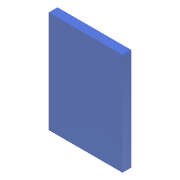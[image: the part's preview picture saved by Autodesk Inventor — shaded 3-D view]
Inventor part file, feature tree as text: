
AUTODESK INVENTOR PART (.ipt)
format: ipt  version: 2014 (Build 180170000, 170)  size: 67,072 bytes
history: native  units: mm
features: extrude x1, sketch x1
ambient origin geometry x8: Origin, YZ Plane, XZ Plane, XY Plane, X Axis, Y Axis, Z Axis, Center Point
bodies: Solid1 (feature_tree)
feature tree (2):
  extrude  "Extrusion1"  Depth=116.0mm
  sketch  "Sketch1"  dims[d0=84.0mm d1=116.0mm d2=10.0mm d3=0.0mm]
